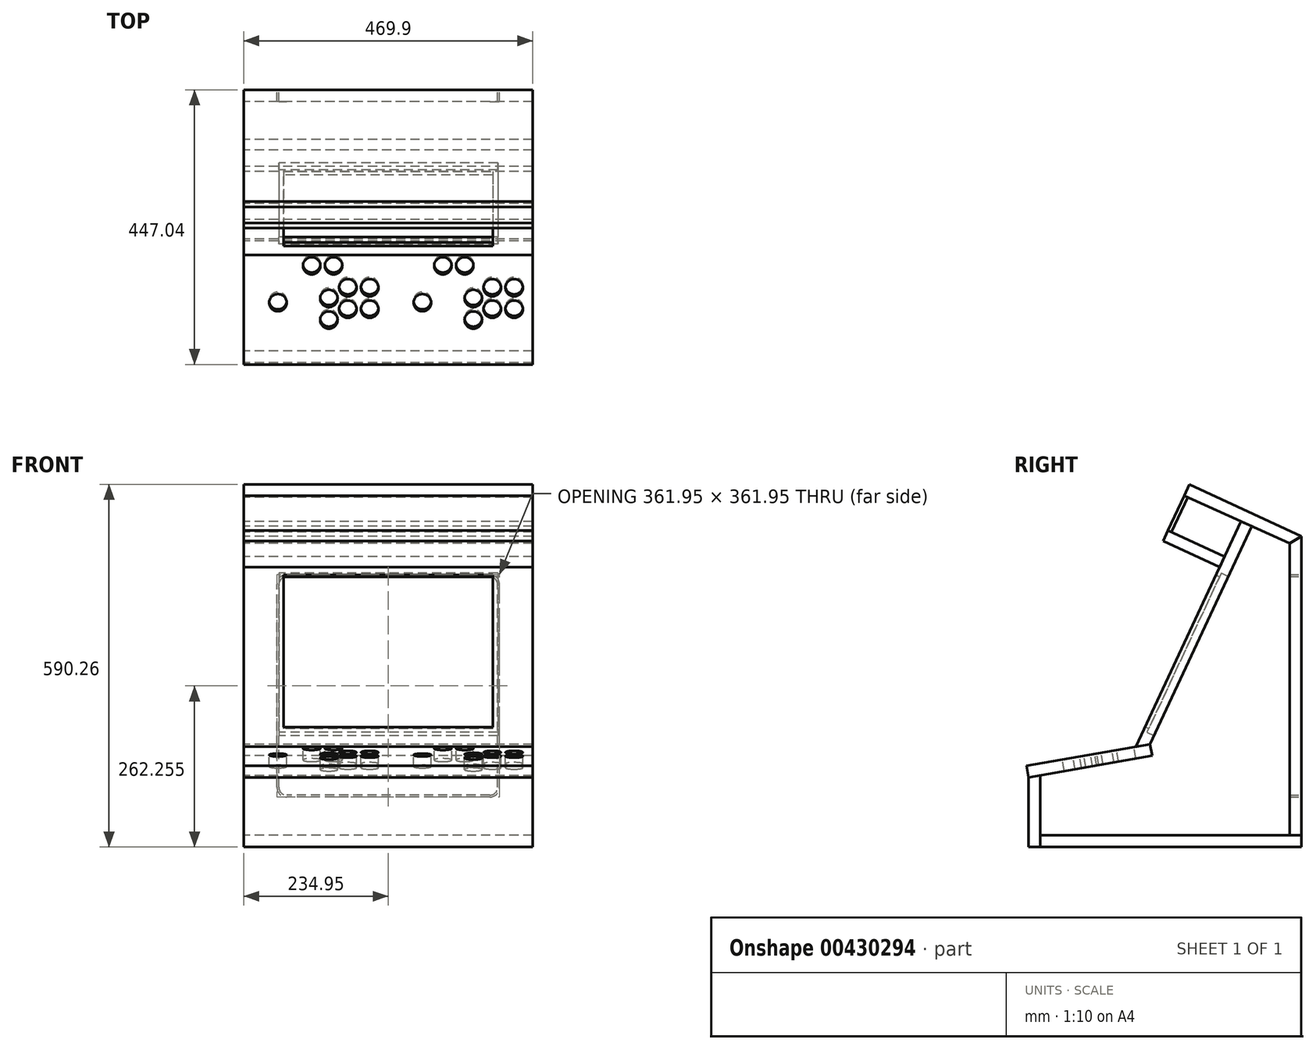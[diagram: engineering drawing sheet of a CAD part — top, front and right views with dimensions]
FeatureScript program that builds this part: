
annotation { "Feature Type Name" : "Feature", "Feature Type Description" : "" }
export const myFeature = defineFeature(function(context is Context, id is Id, definition is map)
    precondition{}
    {
        {
            var Q0;
            Q0=qCreatedBy(makeId("Right.planeOp"),FACE);
            var sketch = newSketch(context, id + "F0", { "sketchPlane" : qUnion([Q0])});
            skLineSegment(sketch, "E0.MirrorCS", {"start": v(265.18, 590.26) * mm, "end": v(222.24, 498.18) * mm, "construction": true});
            skLineSegment(sketch, "E1.MirrorCS", {"start": v(0, 590.26) * mm, "end": v(0, 132.08) * mm, "construction": true});
            skLineSegment(sketch, "E2.MirrorCS", {"start": v(265.18, 590.26) * mm, "end": v(0, 590.26) * mm, "construction": true});
            skLineSegment(sketch, "E3.MirrorCS", {"start": v(447.04, 505.46) * mm, "end": v(265.18, 590.26) * mm});
            skLineSegment(sketch, "E4", {"start": v(447.04, 0) * mm, "end": v(0, 0) * mm, "construction": true});
            skLineSegment(sketch, "E5", {"start": v(0, 0) * mm, "end": v(0, 132.08) * mm, "construction": true});
            skLineSegment(sketch, "E6", {"start": v(222.24, 498.18) * mm, "end": v(222.24, 590.26) * mm, "construction": true});
            skLineSegment(sketch, "E7", {"start": v(0, 132.08) * mm, "end": v(125.07, 154.13) * mm, "construction": true});
            skArc(sketch, "E8", {"start": v(125.07, 154.13) * mm, "mid": v(244.44, 306.17) * mm, "end": v(222.24, 498.18) * mm, "construction": true});
            skLineSegment(sketch, "E9.bottom", {"start": v(447.04, 19.05) * mm, "end": v(428, 19.05) * mm});
            skLineSegment(sketch, "E9.top", {"start": v(447.04, 505.46) * mm, "end": v(428, 494.46) * mm});
            skLineSegment(sketch, "E9.left", {"start": v(447.04, 19.05) * mm, "end": v(447.04, 505.46) * mm});
            skLineSegment(sketch, "E9.right", {"start": v(428, 19.05) * mm, "end": v(428, 494.46) * mm});
            skLineSegment(sketch, "E10", {"start": v(447.04, 0) * mm, "end": v(447.04, 19.05) * mm, "construction": true});
            skLineSegment(sketch, "E11", {"start": v(265.18, 590.26) * mm, "end": v(256.52, 571.7) * mm});
            skLineSegment(sketch, "E12", {"start": v(256.52, 571.7) * mm, "end": v(262.32, 569.1) * mm});
            skLineSegment(sketch, "E13", {"start": v(0, 0) * mm, "end": v(0, 19.05) * mm, "construction": true});
            skLineSegment(sketch, "E14", {"start": v(0, 132.08) * mm, "end": v(178.29, 163.52) * mm});
            skLineSegment(sketch, "E15", {"start": v(204.5, 148.8) * mm, "end": v(3.3, 113.32) * mm});
            skLineSegment(sketch, "E16", {"start": v(3.3, 113.32) * mm, "end": v(0, 132.08) * mm});
            skLineSegment(sketch, "E17.bottom", {"start": v(447.04, 19.05) * mm, "end": v(22.36, 19.05) * mm});
            skLineSegment(sketch, "E17.top", {"start": v(447.04, 0) * mm, "end": v(22.36, 0) * mm});
            skLineSegment(sketch, "E17.left", {"start": v(447.04, 19.05) * mm, "end": v(447.04, 0) * mm});
            skLineSegment(sketch, "E17.right", {"start": v(22.36, 19.05) * mm, "end": v(22.36, 0) * mm});
            skLineSegment(sketch, "E18.bottom", {"start": v(22.36, 0) * mm, "end": v(3.3, 0) * mm});
            skLineSegment(sketch, "E18.top", {"start": v(22.36, 116.68) * mm, "end": v(3.3, 113.32) * mm});
            skLineSegment(sketch, "E18.left", {"start": v(22.36, 0) * mm, "end": v(22.36, 116.68) * mm});
            skLineSegment(sketch, "E18.right", {"start": v(3.3, 0) * mm, "end": v(3.3, 113.32) * mm});
            skLineSegment(sketch, "E19", {"start": v(222.24, 498.18) * mm, "end": v(230.3, 515.45) * mm});
            skLineSegment(sketch, "E20", {"start": v(230.3, 515.45) * mm, "end": v(236.05, 512.76) * mm});
            skLineSegment(sketch, "E21", {"start": v(322.37, 472.5) * mm, "end": v(314.32, 455.24) * mm});
            skLineSegment(sketch, "E22", {"start": v(314.32, 455.24) * mm, "end": v(222.24, 498.18) * mm});
            skLineSegment(sketch, "E23", {"start": v(314.32, 455.24) * mm, "end": v(178.29, 163.52) * mm});
            skLineSegment(sketch, "E24", {"start": v(322.37, 472.5) * mm, "end": v(349.17, 529.97) * mm});
            skLineSegment(sketch, "E25", {"start": v(349.17, 529.97) * mm, "end": v(366.54, 522.14) * mm});
            skLineSegment(sketch, "E26", {"start": v(366.54, 522.14) * mm, "end": v(201.19, 167.56) * mm});
            skLineSegment(sketch, "E27", {"start": v(256.52, 571.7) * mm, "end": v(230.3, 515.45) * mm});
            skLineSegment(sketch, "E28", {"start": v(236.05, 512.76) * mm, "end": v(322.37, 472.5) * mm});
            skLineSegment(sketch, "E29", {"start": v(262.32, 569.1) * mm, "end": v(428, 494.46) * mm});
            skLineSegment(sketch, "E30", {"start": v(262.32, 569.1) * mm, "end": v(236.05, 512.76) * mm});
            skLineSegment(sketch, "E31", {"start": v(178.29, 163.52) * mm, "end": v(201.19, 167.56) * mm});
            skLineSegment(sketch, "E32", {"start": v(201.19, 167.56) * mm, "end": v(201.19, 167.56) * mm});
            skLineSegment(sketch, "E33", {"start": v(201.19, 167.56) * mm, "end": v(204.5, 148.8) * mm});
            skLineSegment(sketch, "E34", {"start": v(349.17, 529.97) * mm, "end": v(178.29, 163.52) * mm, "construction": true});
            skSolve(sketch);
        }
        {
            var Q0;
            Q0=makeQuery(id+"F0.imprint","IMPRINT",FACE,{"disambiguationData":[TD([[makeQuery(id+"F0.imprint","IMPRINT",EDGE,{"derivedFrom":sQuery(id+"F0.wireOp",EDGE,"E9.top")}),1.0]])]});
            extrude(context, id + "F1", {"entities" : qUnion([Q0]), "offsetDistance" : 25.4 * mm, "depth" : 469.9 * mm});
        }
        {
            var Q0;
            Q0=makeQuery(id+"F0.imprint","IMPRINT",FACE,{"disambiguationData":[TD([[makeQuery(id+"F0.imprint","IMPRINT",EDGE,{"derivedFrom":sQuery(id+"F0.wireOp",EDGE,"E3.MirrorCS")}),1.0]])]});
            extrude(context, id + "F2", {"entities" : qUnion([Q0]), "depth" : 469.9 * mm});
        }
        {
            var Q0;
            {var subQ1=sQuery(id+"F0.wireOp",EDGE,"E17.top");Q0=makeQuery(id+"F0.imprint","IMPRINT",FACE,{"disambiguationData":[TD([[makeQuery(id+"F0.imprint","IMPRINT",EDGE,{"derivedFrom":subQ1}),-1.0]])]});}
            extrude(context, id + "F3", {"entities" : qUnion([Q0]), "depth" : 469.9 * mm});
        }
        {
            var Q0;
            {var subQ3=sQuery(id+"F0.wireOp",EDGE,"E18.bottom");Q0=makeQuery(id+"F0.imprint","IMPRINT",FACE,{"disambiguationData":[TD([[makeQuery(id+"F0.imprint","IMPRINT",EDGE,{"derivedFrom":subQ3}),-1.0]])]});}
            extrude(context, id + "F4", {"entities" : qUnion([Q0]), "depth" : 469.9 * mm});
        }
        {
            var Q0;
            Q0=makeQuery(id+"F0.imprint","IMPRINT",FACE,{"disambiguationData":[TD([[makeQuery(id+"F0.imprint","IMPRINT",EDGE,{"derivedFrom":sQuery(id+"F0.wireOp",EDGE,"E14")}),-1.0]])]});
            extrude(context, id + "F5", {"entities" : qUnion([Q0]), "offsetDistance" : 25.4 * mm, "depth" : 469.9 * mm});
        }
        {
            var Q0;
            Q0=makeQuery(id+"F0.imprint","IMPRINT",FACE,{"disambiguationData":[TD([[makeQuery(id+"F0.imprint","IMPRINT",EDGE,{"derivedFrom":sQuery(id+"F0.wireOp",EDGE,"E21")}),1.0]])]});
            extrude(context, id + "F6", {"entities" : qUnion([Q0]), "offsetDistance" : 25.4 * mm, "depth" : 469.9 * mm});
        }
        {
            var Q0;
            Q0=makeQuery(id+"F0.imprint","IMPRINT",FACE,{"disambiguationData":[TD([[makeQuery(id+"F0.imprint","IMPRINT",EDGE,{"derivedFrom":sQuery(id+"F0.wireOp",EDGE,"E19")}),-1.0]])]});
            extrude(context, id + "F7", {"entities" : qUnion([Q0]), "depth" : 469.9 * mm});
        }
        {
            var Q0;
            Q0=makeQuery(id+"F0.imprint","IMPRINT",FACE,{"disambiguationData":[TD([[makeQuery(id+"F0.imprint","IMPRINT",EDGE,{"derivedFrom":sQuery(id+"F0.wireOp",EDGE,"E12")}),-1.0]])]});
            extrude(context, id + "F8", {"entities" : qUnion([Q0]), "offsetDistance" : 25.4 * mm, "depth" : 469.9 * mm});
        }
        {
            var Q0;
            Q0=makeQuery(id+"F5.opExtrude","SWEPT_FACE",FACE,{"disambiguationData":[OSD([sQuery(id+"F0.wireOp",EDGE,"E14")])]});
            var sketch = newSketch(context, id + "F9", { "sketchPlane" : qUnion([Q0])});
            skCircle(sketch, "E35", {"center": v(55.56, 125.08) * mm, "radius": 14.29 * mm});
            skLineSegment(sketch, "E36.bottom", {"start": v(15.88, 80.63) * mm, "end": v(95.25, 80.63) * mm});
            skLineSegment(sketch, "E36.top", {"start": v(15.88, 169.53) * mm, "end": v(95.25, 169.53) * mm});
            skLineSegment(sketch, "E36.left", {"start": v(15.87, 80.63) * mm, "end": v(15.87, 169.53) * mm});
            skLineSegment(sketch, "E36.right", {"start": v(95.25, 80.63) * mm, "end": v(95.25, 169.53) * mm});
            skPoint(sketch, "E37.positionSnap0", {"position": v(95.25, 125.08) * mm});
            skPoint(sketch, "E37.positionSnap1", {"position": v(55.56, 80.63) * mm});
            skCircle(sketch, "E38", {"center": v(138.43, 96.5) * mm, "radius": 14.29 * mm});
            skCircle(sketch, "E39", {"center": v(138.43, 132.07) * mm, "radius": 14.29 * mm});
            skCircle(sketch, "E40", {"center": v(204.79, 149.85) * mm, "radius": 14.29 * mm});
            skCircle(sketch, "E41", {"center": v(169.23, 114.29) * mm, "radius": 14.29 * mm});
            skCircle(sketch, "E42", {"center": v(169.23, 149.85) * mm, "radius": 14.29 * mm});
            skCircle(sketch, "E43", {"center": v(204.79, 114.29) * mm, "radius": 14.29 * mm});
            skLineSegment(sketch, "E44", {"start": v(138.43, 96.5) * mm, "end": v(138.43, 125.08) * mm, "construction": true});
            skLineSegment(sketch, "E45", {"start": v(55.56, 125.08) * mm, "end": v(138.43, 125.08) * mm, "construction": true});
            skLineSegment(sketch, "E46", {"start": v(138.43, 96.5) * mm, "end": v(138.43, 132.07) * mm, "construction": true});
            skLineSegment(sketch, "E47", {"start": v(138.43, 132.07) * mm, "end": v(169.23, 149.85) * mm, "construction": true});
            skLineSegment(sketch, "E48", {"start": v(169.23, 149.85) * mm, "end": v(204.79, 149.85) * mm, "construction": true});
            skLineSegment(sketch, "E49", {"start": v(204.79, 149.85) * mm, "end": v(204.79, 114.29) * mm, "construction": true});
            skLineSegment(sketch, "E50", {"start": v(169.23, 149.85) * mm, "end": v(169.23, 114.29) * mm, "construction": true});
            skLineSegment(sketch, "E51", {"start": v(138.43, 132.07) * mm, "end": v(169.23, 114.29) * mm, "construction": true});
            skPoint(sketch, "E52", {"position": v(219.08, 114.29) * mm});
            skLineSegment(sketch, "E53", {"start": v(15.88, 80.63) * mm, "end": v(219.08, 80.63) * mm, "construction": true});
            skPoint(sketch, "E54", {"position": v(117.48, 80.63) * mm});
            skPoint(sketch, "E55", {"position": v(15.87, 125.08) * mm});
            skLineSegment(sketch, "E56", {"start": v(0, 125.08) * mm, "end": v(234.95, 125.08) * mm, "construction": true});
            skLineSegment(sketch, "E57", {"start": v(234.95, 125.08) * mm, "end": v(469.9, 125.08) * mm, "construction": true});
            skLineSegment(sketch, "E58", {"start": v(117.47, 125.08) * mm, "end": v(117.47, 22.94) * mm, "construction": true});
            skLineSegment(sketch, "E59", {"start": v(352.43, 125.08) * mm, "end": v(352.43, 22.94) * mm, "construction": true});
            skCircle(sketch, "E60", {"center": v(290.51, 125.08) * mm, "radius": 14.29 * mm});
            skLineSegment(sketch, "E61.bottom", {"start": v(250.82, 80.63) * mm, "end": v(330.2, 80.63) * mm});
            skLineSegment(sketch, "E61.top", {"start": v(250.82, 169.53) * mm, "end": v(330.2, 169.53) * mm});
            skLineSegment(sketch, "E61.left", {"start": v(250.83, 80.63) * mm, "end": v(250.83, 169.53) * mm});
            skLineSegment(sketch, "E61.right", {"start": v(330.2, 80.63) * mm, "end": v(330.2, 169.53) * mm});
            skPoint(sketch, "E62.positionSnap0", {"position": v(330.2, 125.08) * mm});
            skPoint(sketch, "E62.positionSnap1", {"position": v(290.51, 80.63) * mm});
            skCircle(sketch, "E63", {"center": v(373.38, 96.5) * mm, "radius": 14.29 * mm});
            skCircle(sketch, "E64", {"center": v(373.38, 132.07) * mm, "radius": 14.29 * mm});
            skCircle(sketch, "E65", {"center": v(439.74, 149.85) * mm, "radius": 14.29 * mm});
            skCircle(sketch, "E66", {"center": v(404.18, 114.29) * mm, "radius": 14.29 * mm});
            skCircle(sketch, "E67", {"center": v(404.18, 149.85) * mm, "radius": 14.29 * mm});
            skCircle(sketch, "E68", {"center": v(439.74, 114.29) * mm, "radius": 14.29 * mm});
            skLineSegment(sketch, "E69", {"start": v(373.38, 96.5) * mm, "end": v(373.38, 125.08) * mm, "construction": true});
            skLineSegment(sketch, "E70", {"start": v(290.51, 125.08) * mm, "end": v(373.38, 125.08) * mm, "construction": true});
            skLineSegment(sketch, "E71", {"start": v(373.38, 96.5) * mm, "end": v(373.38, 132.07) * mm, "construction": true});
            skLineSegment(sketch, "E72", {"start": v(373.38, 132.07) * mm, "end": v(404.18, 149.85) * mm, "construction": true});
            skLineSegment(sketch, "E73", {"start": v(404.18, 149.85) * mm, "end": v(439.74, 149.85) * mm, "construction": true});
            skLineSegment(sketch, "E74", {"start": v(439.74, 149.85) * mm, "end": v(439.74, 114.29) * mm, "construction": true});
            skLineSegment(sketch, "E75", {"start": v(404.18, 149.85) * mm, "end": v(404.18, 114.29) * mm, "construction": true});
            skLineSegment(sketch, "E76", {"start": v(373.38, 132.07) * mm, "end": v(404.18, 114.29) * mm, "construction": true});
            skPoint(sketch, "E77", {"position": v(454.03, 114.29) * mm});
            skLineSegment(sketch, "E78", {"start": v(250.82, 80.63) * mm, "end": v(454.03, 80.63) * mm, "construction": true});
            skPoint(sketch, "E79", {"position": v(352.43, 80.63) * mm});
            skPoint(sketch, "E80", {"position": v(250.83, 125.08) * mm});
            skLineSegment(sketch, "E81", {"start": v(234.95, 22.94) * mm, "end": v(234.95, 125.08) * mm, "construction": true});
            skCircle(sketch, "E82", {"center": v(110.5, 186.04) * mm, "radius": 14.29 * mm});
            skLineSegment(sketch, "E83", {"start": v(234.95, 186.04) * mm, "end": v(323.85, 186.04) * mm, "construction": true});
            skLineSegment(sketch, "E84", {"start": v(323.85, 186.04) * mm, "end": v(359.41, 186.04) * mm, "construction": true});
            skLineSegment(sketch, "E85", {"start": v(234.95, 186.04) * mm, "end": v(146.05, 186.04) * mm, "construction": true});
            skLineSegment(sketch, "E86", {"start": v(146.05, 186.04) * mm, "end": v(110.5, 186.04) * mm, "construction": true});
            skCircle(sketch, "E87", {"center": v(146.05, 186.04) * mm, "radius": 14.29 * mm});
            skCircle(sketch, "E88", {"center": v(323.85, 186.04) * mm, "radius": 14.29 * mm});
            skCircle(sketch, "E89", {"center": v(359.41, 186.04) * mm, "radius": 14.29 * mm});
            skLineSegment(sketch, "E90", {"start": v(234.95, 125.08) * mm, "end": v(234.95, 269.51) * mm, "construction": true});
            skSolve(sketch);
        }
        {
            var Q0;
            Q0=makeQuery(id+"F9.imprint","IMPRINT",FACE,{"disambiguationData":[TD([[makeQuery(id+"F9.imprint","IMPRINT",EDGE,{"derivedFrom":sQuery(id+"F9.wireOp",EDGE,"E39")}),1.0]])]});
            var Q1;
            Q1=makeQuery(id+"F9.imprint","IMPRINT",FACE,{"disambiguationData":[TD([[makeQuery(id+"F9.imprint","IMPRINT",EDGE,{"derivedFrom":sQuery(id+"F9.wireOp",EDGE,"E38")}),1.0]])]});
            var Q2;
            Q2=makeQuery(id+"F9.imprint","IMPRINT",FACE,{"disambiguationData":[TD([[makeQuery(id+"F9.imprint","IMPRINT",EDGE,{"derivedFrom":sQuery(id+"F9.wireOp",EDGE,"E41")}),1.0]])]});
            var Q3;
            Q3=makeQuery(id+"F9.imprint","IMPRINT",FACE,{"disambiguationData":[TD([[makeQuery(id+"F9.imprint","IMPRINT",EDGE,{"derivedFrom":sQuery(id+"F9.wireOp",EDGE,"E42")}),1.0]])]});
            var Q4;
            Q4=makeQuery(id+"F9.imprint","IMPRINT",FACE,{"disambiguationData":[TD([[makeQuery(id+"F9.imprint","IMPRINT",EDGE,{"derivedFrom":sQuery(id+"F9.wireOp",EDGE,"E40")}),1.0]])]});
            var Q5;
            Q5=makeQuery(id+"F9.imprint","IMPRINT",FACE,{"disambiguationData":[TD([[makeQuery(id+"F9.imprint","IMPRINT",EDGE,{"derivedFrom":sQuery(id+"F9.wireOp",EDGE,"E43")}),1.0]])]});
            var Q6;
            Q6=makeQuery(id+"F9.imprint","IMPRINT",FACE,{"disambiguationData":[TD([[makeQuery(id+"F9.imprint","IMPRINT",EDGE,{"derivedFrom":sQuery(id+"F9.wireOp",EDGE,"E82")}),1.0]])]});
            var Q7;
            Q7=makeQuery(id+"F9.imprint","IMPRINT",FACE,{"disambiguationData":[TD([[makeQuery(id+"F9.imprint","IMPRINT",EDGE,{"derivedFrom":sQuery(id+"F9.wireOp",EDGE,"E87")}),1.0]])]});
            var Q8;
            Q8=makeQuery(id+"F9.imprint","IMPRINT",FACE,{"disambiguationData":[TD([[makeQuery(id+"F9.imprint","IMPRINT",EDGE,{"derivedFrom":sQuery(id+"F9.wireOp",EDGE,"E35")}),1.0]])]});
            var Q9;
            Q9=makeQuery(id+"F9.imprint","IMPRINT",FACE,{"disambiguationData":[TD([[makeQuery(id+"F9.imprint","IMPRINT",EDGE,{"derivedFrom":sQuery(id+"F9.wireOp",EDGE,"E88")}),1.0]])]});
            var Q10;
            Q10=makeQuery(id+"F9.imprint","IMPRINT",FACE,{"disambiguationData":[TD([[makeQuery(id+"F9.imprint","IMPRINT",EDGE,{"derivedFrom":sQuery(id+"F9.wireOp",EDGE,"E89")}),1.0]])]});
            var Q11;
            Q11=makeQuery(id+"F9.imprint","IMPRINT",FACE,{"disambiguationData":[TD([[makeQuery(id+"F9.imprint","IMPRINT",EDGE,{"derivedFrom":sQuery(id+"F9.wireOp",EDGE,"E60")}),1.0]])]});
            var Q12;
            Q12=makeQuery(id+"F9.imprint","IMPRINT",FACE,{"disambiguationData":[TD([[makeQuery(id+"F9.imprint","IMPRINT",EDGE,{"derivedFrom":sQuery(id+"F9.wireOp",EDGE,"E63")}),1.0]])]});
            var Q13;
            Q13=makeQuery(id+"F9.imprint","IMPRINT",FACE,{"disambiguationData":[TD([[makeQuery(id+"F9.imprint","IMPRINT",EDGE,{"derivedFrom":sQuery(id+"F9.wireOp",EDGE,"E64")}),1.0]])]});
            var Q14;
            Q14=makeQuery(id+"F9.imprint","IMPRINT",FACE,{"disambiguationData":[TD([[makeQuery(id+"F9.imprint","IMPRINT",EDGE,{"derivedFrom":sQuery(id+"F9.wireOp",EDGE,"E66")}),1.0]])]});
            var Q15;
            Q15=makeQuery(id+"F9.imprint","IMPRINT",FACE,{"disambiguationData":[TD([[makeQuery(id+"F9.imprint","IMPRINT",EDGE,{"derivedFrom":sQuery(id+"F9.wireOp",EDGE,"E67")}),1.0]])]});
            var Q16;
            Q16=makeQuery(id+"F9.imprint","IMPRINT",FACE,{"disambiguationData":[TD([[makeQuery(id+"F9.imprint","IMPRINT",EDGE,{"derivedFrom":sQuery(id+"F9.wireOp",EDGE,"E65")}),1.0]])]});
            var Q17;
            Q17=makeQuery(id+"F9.imprint","IMPRINT",FACE,{"disambiguationData":[TD([[makeQuery(id+"F9.imprint","IMPRINT",EDGE,{"derivedFrom":sQuery(id+"F9.wireOp",EDGE,"E68")}),1.0]])]});
            extrude(context, id + "F10", {"entities" : qUnion([Q0, Q1, Q2, Q3, Q4, Q5, Q6, Q7, Q8, Q9, Q10, Q11, Q12, Q13, Q14, Q15, Q16, Q17]), "operationType" : NewBodyOperationType.REMOVE, "oppositeDirection" : true, "offsetDistance" : 25.4 * mm, "depth" : 19.05 * mm});
        }
        {
            var Q0;
            Q0=makeQuery(id+"F6.opExtrude","SWEPT_FACE",FACE,{"disambiguationData":[OSD([sQuery(id+"F0.wireOp",EDGE,"E21"),sQuery(id+"F0.wireOp",EDGE,"E23"),sQuery(id+"F0.wireOp",EDGE,"E24")])]});
            var sketch = newSketch(context, id + "F11", { "sketchPlane" : qUnion([Q0])});
            skLineSegment(sketch, "E91", {"start": v(469.9, 425.71) * mm, "end": v(0, 425.71) * mm, "construction": true});
            skLineSegment(sketch, "E92", {"start": v(234.95, 627.88) * mm, "end": v(234.95, 223.54) * mm, "construction": true});
            skLineSegment(sketch, "E93.bottom", {"start": v(405.13, 531.52) * mm, "end": v(64.77, 531.52) * mm});
            skLineSegment(sketch, "E93.top", {"start": v(405.13, 258.47) * mm, "end": v(64.77, 258.47) * mm});
            skLineSegment(sketch, "E93.left", {"start": v(405.13, 531.52) * mm, "end": v(405.13, 258.47) * mm});
            skLineSegment(sketch, "E93.right", {"start": v(64.77, 531.52) * mm, "end": v(64.77, 258.47) * mm});
            skPoint(sketch, "E93.middle", {"position": v(234.95, 395) * mm});
            skPoint(sketch, "E94", {"position": v(234.95, 425.71) * mm});
            skSolve(sketch);
        }
        {
            var Q0;
            Q0=makeQuery(id+"F11.imprint","IMPRINT",FACE,{"disambiguationData":[TD([[makeQuery(id+"F11.imprint","IMPRINT",EDGE,{"derivedFrom":sQuery(id+"F11.wireOp",EDGE,"E93.bottom")}),1.0]])]});
            extrude(context, id + "F12", {"entities" : qUnion([Q0]), "operationType" : NewBodyOperationType.REMOVE, "oppositeDirection" : true, "depth" : 19.05 * mm});
        }
        {
            var Q0;
            Q0=makeQuery(id+"F1.opExtrude","SWEPT_FACE",FACE,{"disambiguationData":[OSD([sQuery(id+"F0.wireOp",EDGE,"E9.left")])]});
            var sketch = newSketch(context, id + "F13", { "sketchPlane" : qUnion([Q0])});
            skLineSegment(sketch, "E95", {"start": v(0, 19.05) * mm, "end": v(-469.9, 505.46) * mm, "construction": true});
            skLineSegment(sketch, "E96.bottom", {"start": v(-400.05, 84.46) * mm, "end": v(-69.85, 84.46) * mm});
            skLineSegment(sketch, "E96.top", {"start": v(-400.05, 440.06) * mm, "end": v(-69.85, 440.06) * mm});
            skLineSegment(sketch, "E96.left", {"start": v(-412.75, 97.16) * mm, "end": v(-412.75, 427.36) * mm});
            skLineSegment(sketch, "E96.right", {"start": v(-57.15, 97.16) * mm, "end": v(-57.15, 427.36) * mm});
            skPoint(sketch, "E96.middle", {"position": v(-234.95, 262.26) * mm});
            skPoint(sketch, "E97.visualSharp", {"position": v(-412.75, 440.06) * mm});
            skArc(sketch, "E97.filletArc", {"start": v(-400.05, 440.06) * mm, "mid": v(-409.03, 436.34) * mm, "end": v(-412.75, 427.36) * mm});
            skPoint(sketch, "E98.visualSharp", {"position": v(-57.15, 440.06) * mm});
            skArc(sketch, "E98.filletArc", {"start": v(-57.15, 427.36) * mm, "mid": v(-60.87, 436.34) * mm, "end": v(-69.85, 440.05) * mm});
            skPoint(sketch, "E99.visualSharp", {"position": v(-412.75, 84.46) * mm});
            skArc(sketch, "E99.filletArc", {"start": v(-412.75, 97.16) * mm, "mid": v(-409.03, 88.17) * mm, "end": v(-400.05, 84.46) * mm});
            skPoint(sketch, "E100.visualSharp", {"position": v(-57.15, 84.46) * mm});
            skArc(sketch, "E100.filletArc", {"start": v(-69.85, 84.45) * mm, "mid": v(-60.87, 88.17) * mm, "end": v(-57.15, 97.16) * mm});
            skArc(sketch, "E101.0", {"start": v(-69.85, 81.28) * mm, "mid": v(-58.62, 85.93) * mm, "end": v(-53.97, 97.16) * mm});
            skLineSegment(sketch, "E101.1", {"start": v(-400.05, 81.28) * mm, "end": v(-69.85, 81.28) * mm});
            skLineSegment(sketch, "E101.2", {"start": v(-53.97, 97.16) * mm, "end": v(-53.97, 427.36) * mm});
            skArc(sketch, "E101.3", {"start": v(-415.93, 97.16) * mm, "mid": v(-411.28, 85.93) * mm, "end": v(-400.05, 81.28) * mm});
            skArc(sketch, "E101.4", {"start": v(-53.97, 427.36) * mm, "mid": v(-58.62, 438.58) * mm, "end": v(-69.85, 443.23) * mm});
            skLineSegment(sketch, "E101.5", {"start": v(-400.05, 443.23) * mm, "end": v(-69.85, 443.23) * mm});
            skArc(sketch, "E101.6", {"start": v(-400.05, 443.23) * mm, "mid": v(-411.28, 438.58) * mm, "end": v(-415.93, 427.36) * mm});
            skLineSegment(sketch, "E101.7", {"start": v(-415.93, 97.16) * mm, "end": v(-415.93, 427.36) * mm});
            skSolve(sketch);
        }
        {
            var Q0;
            Q0=makeQuery(id+"F13.imprint","IMPRINT",FACE,{"disambiguationData":[TD([[makeQuery(id+"F13.imprint","IMPRINT",EDGE,{"derivedFrom":sQuery(id+"F13.wireOp",EDGE,"E96.bottom")}),-1.0]])]});
            extrude(context, id + "F14", {"entities" : qUnion([Q0]), "operationType" : NewBodyOperationType.REMOVE, "oppositeDirection" : true, "depth" : 19.05 * mm});
        }
        {
            var Q0;
            Q0=makeQuery(id+"F6.opExtrude","SWEPT_FACE",FACE,{"disambiguationData":[OSD([sQuery(id+"F0.wireOp",EDGE,"E26")])]});
            var sketch = newSketch(context, id + "F15", { "sketchPlane" : qUnion([Q0])});
            skLineSegment(sketch, "E102.0", {"start": v(-56.83, 537.87) * mm, "end": v(-56.83, 252.12) * mm});
            skLineSegment(sketch, "E103.0", {"start": v(-413.07, 537.87) * mm, "end": v(-413.07, 252.12) * mm});
            skLineSegment(sketch, "E104.0", {"start": v(-413.07, 537.87) * mm, "end": v(-56.83, 537.87) * mm});
            skLineSegment(sketch, "E105.0", {"start": v(-413.07, 252.12) * mm, "end": v(-56.83, 252.12) * mm});
            skSolve(sketch);
        }
        {
            var Q0;
            Q0=makeQuery(id+"F15.imprint","IMPRINT",FACE,{"disambiguationData":[TD([[makeQuery(id+"F15.imprint","IMPRINT",EDGE,{"derivedFrom":sQuery(id+"F15.wireOp",EDGE,"E102.0")}),-1.0]])]});
            extrude(context, id + "F16", {"entities" : qUnion([Q0]), "operationType" : NewBodyOperationType.REMOVE, "oppositeDirection" : true, "depth" : 12.7 * mm});
        }
    });
